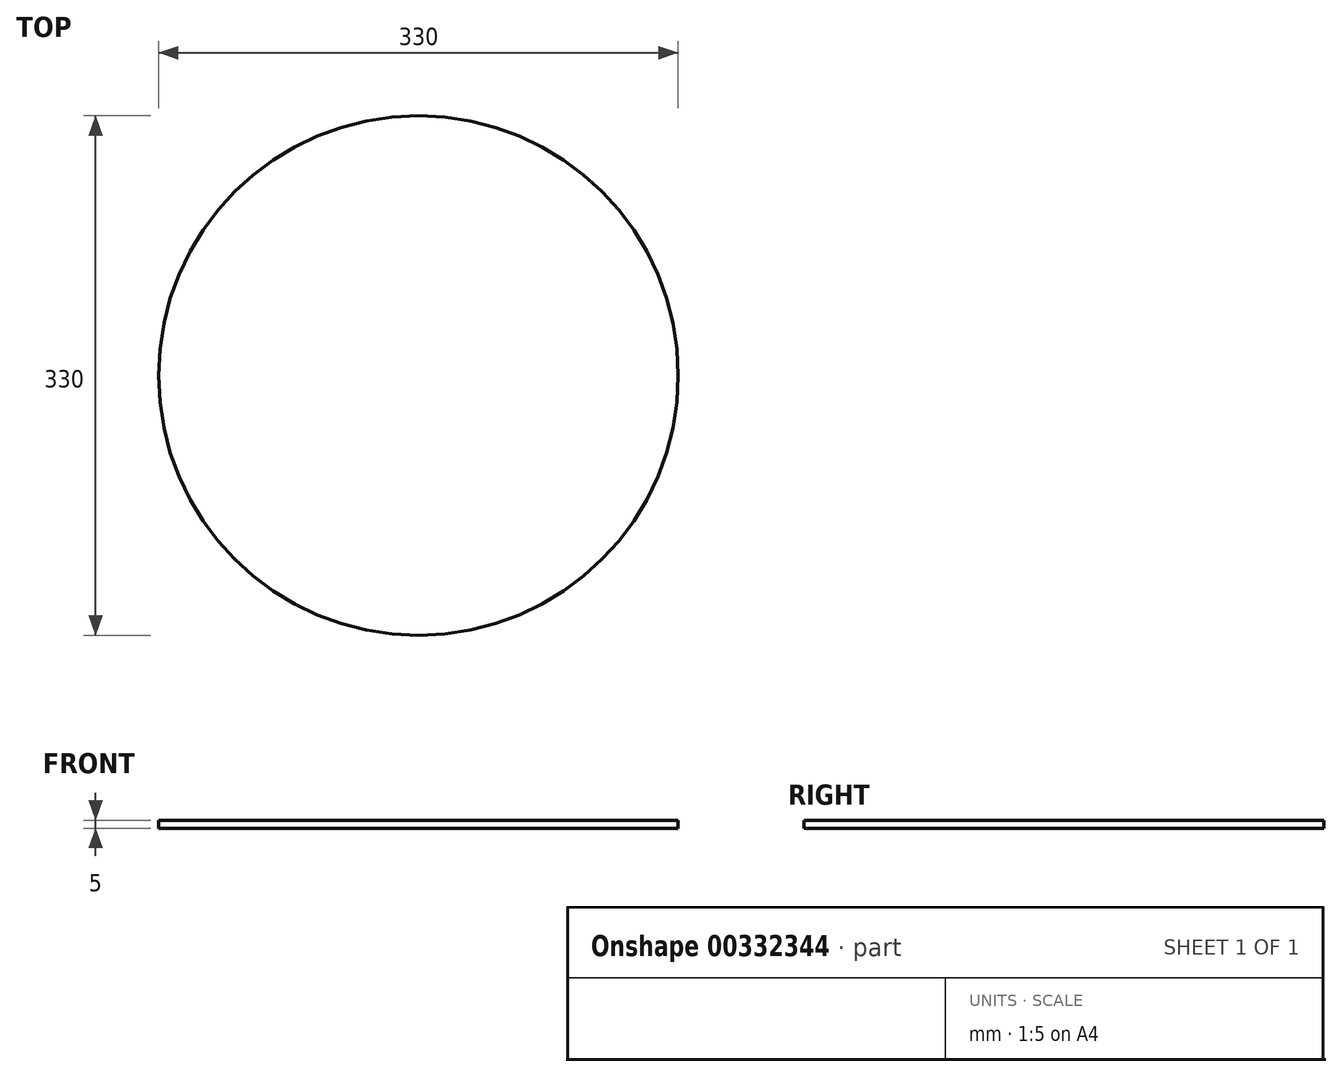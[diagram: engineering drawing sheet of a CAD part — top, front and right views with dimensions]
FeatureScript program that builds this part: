
annotation { "Feature Type Name" : "Feature", "Feature Type Description" : "" }
export const myFeature = defineFeature(function(context is Context, id is Id, definition is map)
    precondition{}
    {
        {
            var Q0;
            Q0=qCreatedBy(makeId("Top.planeOp"),FACE);
            var sketch = newSketch(context, id + "F0", { "sketchPlane" : qUnion([Q0])});
            skCircle(sketch, "E0", {"center": v(0, 0) * mm, "radius": 165 * mm});
            skSolve(sketch);
        }
        {
            var Q0;
            Q0=makeQuery(id+"F0.imprint","IMPRINT",FACE,{"disambiguationData":[TD([[makeQuery(id+"F0.imprint","IMPRINT",EDGE,{"derivedFrom":sQuery(id+"F0.wireOp",EDGE,"E0")}),1.0]])]});
            extrude(context, id + "F1", {"entities" : qUnion([Q0]), "depth" : 5 * mm});
        }
    });
